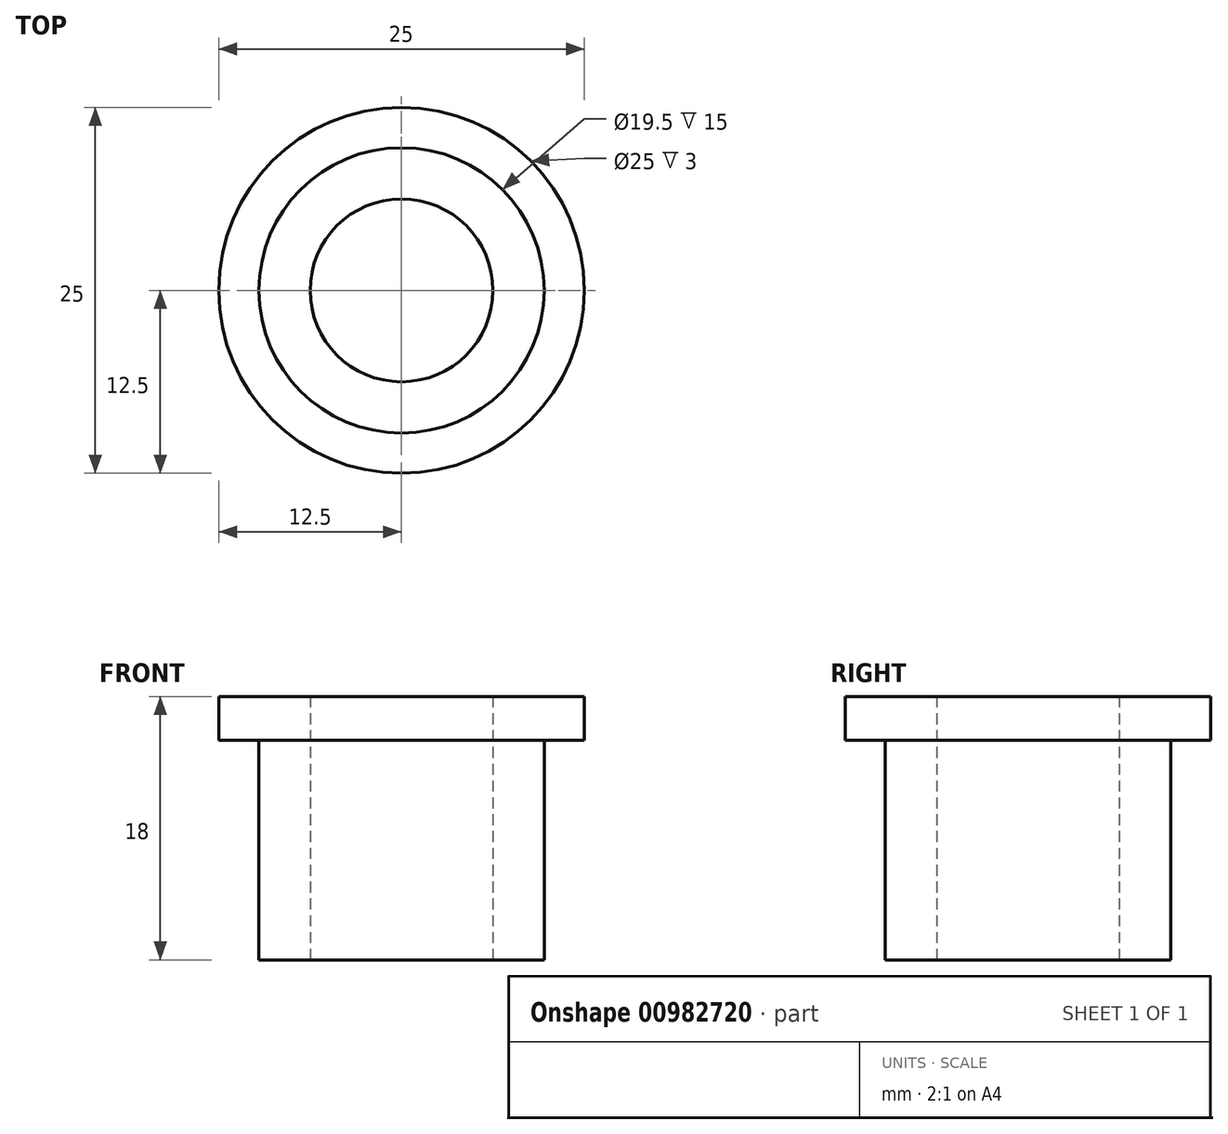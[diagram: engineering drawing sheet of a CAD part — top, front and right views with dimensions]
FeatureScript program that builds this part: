
annotation { "Feature Type Name" : "Feature", "Feature Type Description" : "" }
export const myFeature = defineFeature(function(context is Context, id is Id, definition is map)
    precondition{}
    {
        {
            var Q0;
            Q0=qCreatedBy(makeId("Front.planeOp"),FACE);
            var sketch = newSketch(context, id + "F0", { "sketchPlane" : qUnion([Q0])});
            skLineSegment(sketch, "E0", {"start": v(-6.25, 0) * mm, "end": v(-12.5, 0) * mm});
            skLineSegment(sketch, "E1", {"start": v(-12.5, 0) * mm, "end": v(-12.5, -3) * mm});
            skLineSegment(sketch, "E2", {"start": v(-12.5, -3) * mm, "end": v(-9.75, -3) * mm});
            skLineSegment(sketch, "E3", {"start": v(-9.75, -3) * mm, "end": v(-9.75, -18) * mm});
            skLineSegment(sketch, "E4", {"start": v(-9.75, -18) * mm, "end": v(-6.25, -18) * mm});
            skLineSegment(sketch, "E5", {"start": v(-6.25, -18) * mm, "end": v(-6.25, 0) * mm});
            skLineSegment(sketch, "E6", {"start": v(0, 0) * mm, "end": v(0, -10.96) * mm, "construction": true});
            skSolve(sketch);
        }
        {
            var Q0;
            Q0=sQuery(id+"F0.wireOp",EDGE,"E0");
            var Q1;
            Q1=sQuery(id+"F0.wireOp",EDGE,"E1");
            var Q2;
            Q2=sQuery(id+"F0.wireOp",EDGE,"E2");
            var Q3;
            Q3=sQuery(id+"F0.wireOp",EDGE,"E3");
            var Q4;
            Q4=sQuery(id+"F0.wireOp",EDGE,"E5");
            var Q5;
            Q5=sQuery(id+"F0.wireOp",EDGE,"E4");
            var Q6;
            Q6=sQuery(id+"F0.wireOp",EDGE,"E6");
            revolve(context, id + "F1", {"bodyType" : ToolBodyType.SURFACE, "surfaceOperationType" : NewSurfaceOperationType.NEW, "surfaceEntities" : qUnion([Q0, Q1, Q2, Q3, Q4, Q5]), "axis" : qUnion([Q6]), "revolveType" : RevolveType.FULL});
        }
    });
